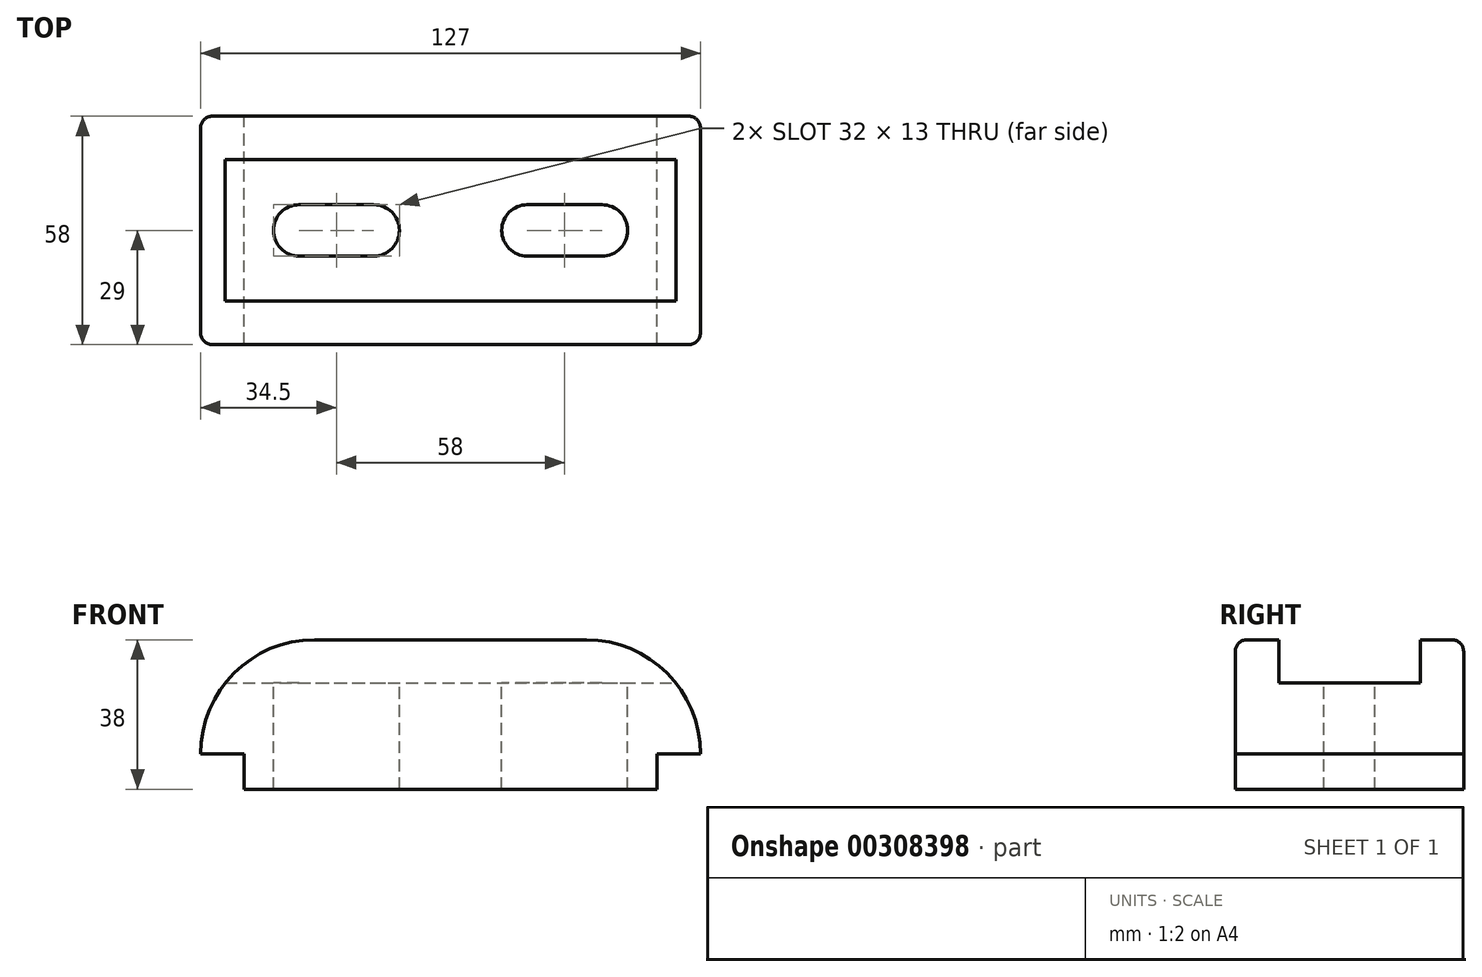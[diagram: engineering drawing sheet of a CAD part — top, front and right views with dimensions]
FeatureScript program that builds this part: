
annotation { "Feature Type Name" : "Feature", "Feature Type Description" : "" }
export const myFeature = defineFeature(function(context is Context, id is Id, definition is map)
    precondition{}
    {
        {
            var Q0;
            Q0=qCreatedBy(makeId("Front.planeOp"),FACE);
            var sketch = newSketch(context, id + "F0", { "sketchPlane" : qUnion([Q0])});
            skLineSegment(sketch, "E0", {"start": v(0, 0) * mm, "end": v(0, 9) * mm});
            skLineSegment(sketch, "E1", {"start": v(0, 9) * mm, "end": v(-11, 9) * mm});
            skLineSegment(sketch, "E2", {"start": v(0, 0) * mm, "end": v(105, 0) * mm});
            skLineSegment(sketch, "E3", {"start": v(105, 0) * mm, "end": v(105, 9) * mm});
            skLineSegment(sketch, "E4", {"start": v(105, 9) * mm, "end": v(116, 9) * mm});
            skArc(sketch, "E5", {"start": v(18, 38) * mm, "mid": v(-2.5, 29.5) * mm, "end": v(-11, 9) * mm});
            skArc(sketch, "E6", {"start": v(116, 9) * mm, "mid": v(107.5, 29.5) * mm, "end": v(87, 38) * mm});
            skLineSegment(sketch, "E7", {"start": v(18, 38) * mm, "end": v(87, 38) * mm});
            skLineSegment(sketch, "E8", {"start": v(0, 9) * mm, "end": v(105, 9) * mm, "construction": true});
            skSolve(sketch);
        }
        {
            var Q0;
            Q0 = qSketchRegion(id + "F0", true);
            extrude(context, id + "F1", {"entities" : qUnion([Q0]), "depth" : 58 * mm});
        }
        {
            var Q0;
            Q0=makeQuery(id+"F1.opExtrude","SWEPT_FACE",FACE,{"disambiguationData":[OSD([sQuery(id+"F0.wireOp",EDGE,"E7")])]});
            var sketch = newSketch(context, id + "F2", { "sketchPlane" : qUnion([Q0])});
            skLineSegment(sketch, "E9.bottom", {"start": v(-11, -11) * mm, "end": v(116, -11) * mm});
            skLineSegment(sketch, "E9.top", {"start": v(-11, -47) * mm, "end": v(116, -47) * mm});
            skLineSegment(sketch, "E9.left", {"start": v(-11, -11) * mm, "end": v(-11, -47) * mm});
            skLineSegment(sketch, "E9.right", {"start": v(116, -11) * mm, "end": v(116, -47) * mm});
            skPoint(sketch, "E10.0", {"position": v(-11, -29) * mm});
            skSolve(sketch);
        }
        {
            var Q0;
            Q0 = qSketchRegion(id + "F2", true);
            extrude(context, id + "F3", {"entities" : qUnion([Q0]), "operationType" : NewBodyOperationType.REMOVE, "oppositeDirection" : true, "depth" : 11 * mm});
        }
        {
            var Q0;
            Q0=makeQuery(id+"F3.boolean.opBoolean","COPY",FACE,{"derivedFrom":makeQuery(id+"F3.opExtrude","CAP_FACE",FACE,{"disambiguationData":[OSD([sQuery(id+"F2.wireOp",EDGE,"E9.bottom"),sQuery(id+"F2.wireOp",EDGE,"E9.top"),sQuery(id+"F2.wireOp",EDGE,"E9.left"),sQuery(id+"F2.wireOp",EDGE,"E9.right")])],"isStart":false})});
            var sketch = newSketch(context, id + "F4", { "sketchPlane" : qUnion([Q0])});
            skLineSegment(sketch, "E11", {"start": v(14, -29) * mm, "end": v(33, -29) * mm, "construction": true});
            skPoint(sketch, "E11.startSnap0", {"position": v(-4.74, -29) * mm});
            skArc(sketch, "E12.0.startCap", {"start": v(14, -35.5) * mm, "mid": v(7.5, -29) * mm, "end": v(14, -22.5) * mm});
            skArc(sketch, "E12.0.endCap", {"start": v(33, -22.5) * mm, "mid": v(39.5, -29) * mm, "end": v(33, -35.5) * mm});
            skLineSegment(sketch, "E12.0.left", {"start": v(14, -22.5) * mm, "end": v(33, -22.5) * mm});
            skLineSegment(sketch, "E12.0.right", {"start": v(14, -35.5) * mm, "end": v(33, -35.5) * mm});
            skLineSegment(sketch, "E13", {"start": v(52.5, -11) * mm, "end": v(52.5, -47) * mm, "construction": true});
            skArc(sketch, "E14.MirrorCS", {"start": v(91, -35.5) * mm, "mid": v(97.5, -29) * mm, "end": v(91, -22.5) * mm});
            skLineSegment(sketch, "E15.MirrorCS", {"start": v(91, -29) * mm, "end": v(72, -29) * mm, "construction": true});
            skLineSegment(sketch, "E16.MirrorCS", {"start": v(91, -22.5) * mm, "end": v(72, -22.5) * mm});
            skLineSegment(sketch, "E17.MirrorCS", {"start": v(91, -35.5) * mm, "end": v(72, -35.5) * mm});
            skArc(sketch, "E18.MirrorCS", {"start": v(72, -22.5) * mm, "mid": v(65.5, -29) * mm, "end": v(72, -35.5) * mm});
            skSolve(sketch);
        }
        {
            var Q0;
            Q0 = qSketchRegion(id + "F4", true);
            extrude(context, id + "F5", {"entities" : qUnion([Q0]), "operationType" : NewBodyOperationType.REMOVE, "endBound" : BoundingType.THROUGH_ALL, "oppositeDirection" : true, "depth" : 25 * mm});
        }
        {
            var Q0;
            Q0=makeQuery(id+"F1.opExtrude","CAP_EDGE",EDGE,{"disambiguationData":[OSD([sQuery(id+"F0.wireOp",EDGE,"E7")])],"isStart":false});
            var Q1;
            Q1=makeQuery(id+"F1.opExtrude","CAP_EDGE",EDGE,{"disambiguationData":[OSD([sQuery(id+"F0.wireOp",EDGE,"E6")])],"isStart":true});
            fillet(context, id + "F6", {"entities" : qUnion([Q0, Q1]), "radius" : 3 * mm, "tangentPropagation" : true, "allowEdgeOverflow" : false});
        }
    });
